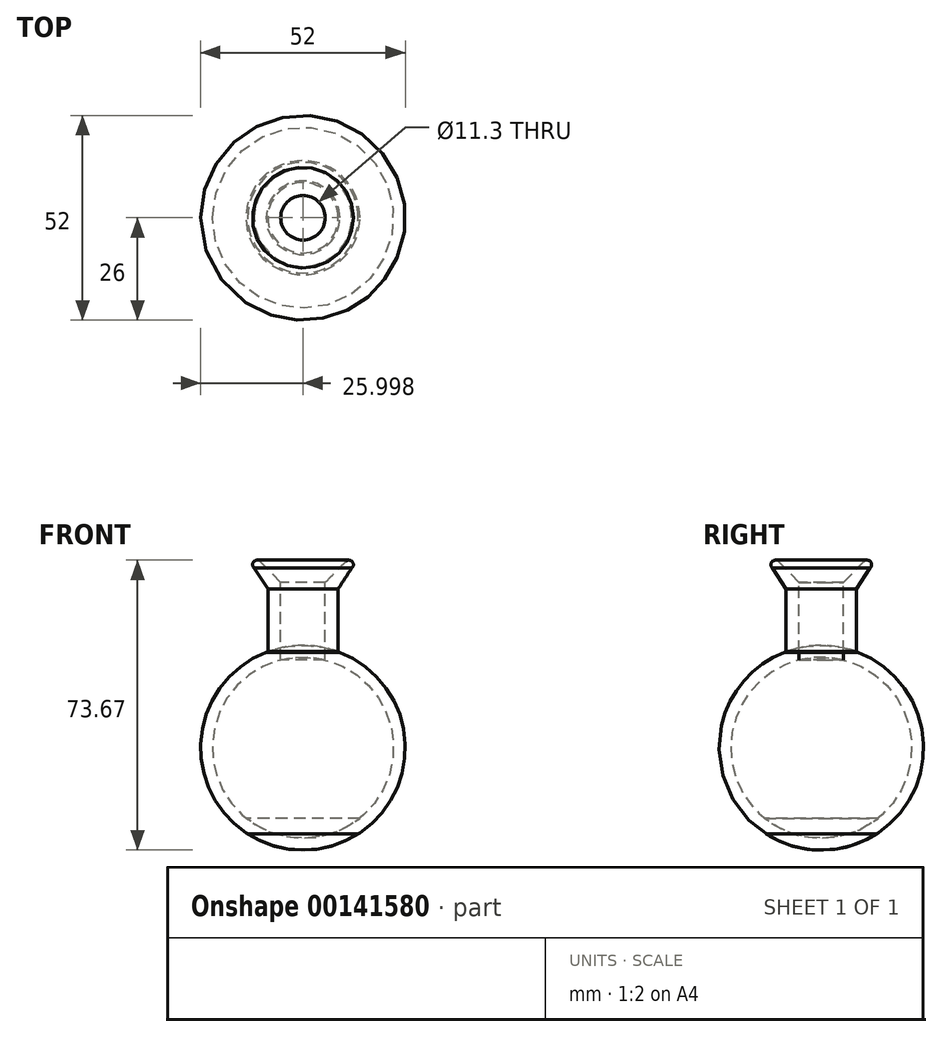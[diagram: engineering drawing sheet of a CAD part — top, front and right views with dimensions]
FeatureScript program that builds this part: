
annotation { "Feature Type Name" : "Feature", "Feature Type Description" : "" }
export const myFeature = defineFeature(function(context is Context, id is Id, definition is map)
    precondition{}
    {
        {
            var Q0;
            Q0=qCreatedBy(makeId("Front.planeOp"),FACE);
            var sketch = newSketch(context, id + "F0", { "sketchPlane" : qUnion([Q0])});
            skLineSegment(sketch, "E0.right", {"start": v(8.93, 40.36) * mm, "end": v(8.93, 24.42) * mm});
            skArc(sketch, "E1", {"start": v(14.04, -21.88) * mm, "mid": v(25.87, 2.63) * mm, "end": v(9.35, 24.26) * mm});
            skLineSegment(sketch, "E2", {"start": v(0, -21.88) * mm, "end": v(14.04, -21.88) * mm});
            skPoint(sketch, "E3.visualSharp", {"position": v(8.93, 42.42) * mm});
            skLineSegment(sketch, "E4", {"start": v(10.85, 47.33) * mm, "end": v(5.65, 41.97) * mm});
            skLineSegment(sketch, "E5", {"start": v(5.65, 41.97) * mm, "end": v(5.65, 22.3) * mm});
            skArc(sketch, "E6", {"start": v(12.38, 45.66) * mm, "mid": v(12.5, 47.3) * mm, "end": v(10.85, 47.33) * mm});
            skLineSegment(sketch, "E7", {"start": v(14.46, -17.88) * mm, "end": v(0, -17.88) * mm});
            skLineSegment(sketch, "E8", {"start": v(0, -17.88) * mm, "end": v(0, -21.88) * mm});
            skArc(sketch, "E9", {"start": v(14.46, -17.88) * mm, "mid": v(22.47, 4.93) * mm, "end": v(5.65, 22.3) * mm});
            skLineSegment(sketch, "E10", {"start": v(8.93, 24.42) * mm, "end": v(9.35, 24.26) * mm});
            skLineSegment(sketch, "E11", {"start": v(12.38, 45.66) * mm, "end": v(8.93, 40.36) * mm});
            skSolve(sketch);
        }
        {
            var Q0;
            Q0=qSketchRegion(id+"F0",true);
            var Q1;
            Q1=sQuery(id+"F0.wireOp",EDGE,"E8");
            revolve(context, id + "F1", {"entities" : qUnion([Q0]), "axis" : qUnion([Q1]), "revolveType" : RevolveType.FULL});
        }
    });
